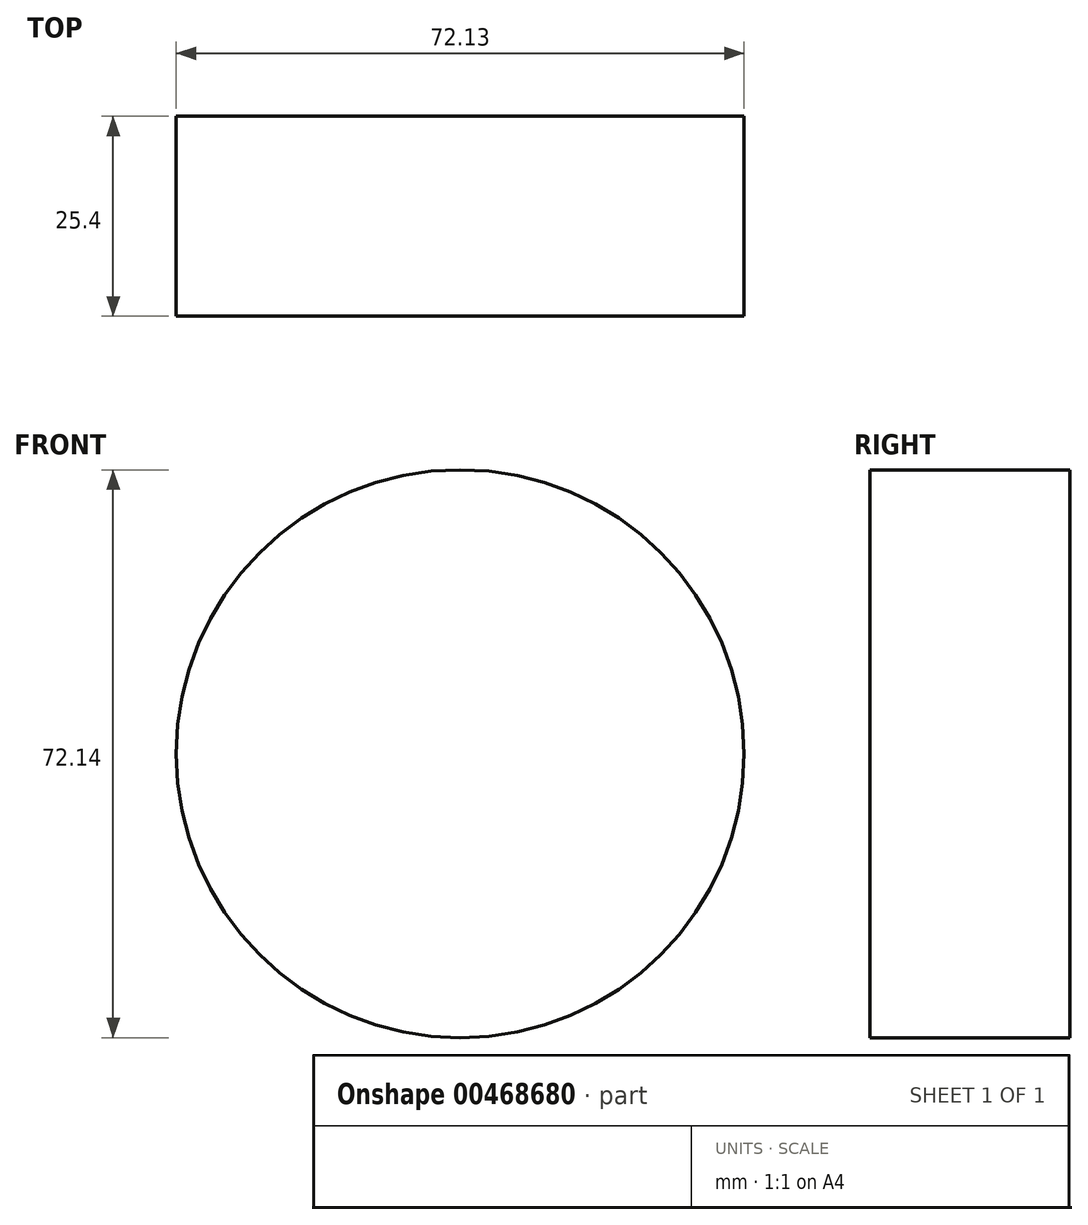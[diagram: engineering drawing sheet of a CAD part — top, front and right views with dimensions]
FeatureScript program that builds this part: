
annotation { "Feature Type Name" : "Feature", "Feature Type Description" : "" }
export const myFeature = defineFeature(function(context is Context, id is Id, definition is map)
    precondition{}
    {
        {
            var Q0;
            Q0=qCreatedBy(makeId("Front.planeOp"),FACE);
            var sketch = newSketch(context, id + "F0", { "sketchPlane" : qUnion([Q0])});
            skCircle(sketch, "E0", {"center": v(0, 0) * mm, "radius": 25.64 * mm});
            skCircle(sketch, "E1", {"center": v(-54.61, 52.2) * mm, "radius": 16.14 * mm});
            skCircle(sketch, "E2", {"center": v(-55.11, -69.72) * mm, "radius": 36.07 * mm});
            skSolve(sketch);
        }
        {
            var Q0;
            Q0=makeQuery(id+"F0.imprint","IMPRINT",FACE,{"disambiguationData":[TD([[makeQuery(id+"F0.imprint","IMPRINT",EDGE,{"derivedFrom":sQuery(id+"F0.wireOp",EDGE,"E2")}),1.0]])]});
            extrude(context, id + "F1", {"entities" : qUnion([Q0]), "depth" : 25.4 * mm});
        }
    });
